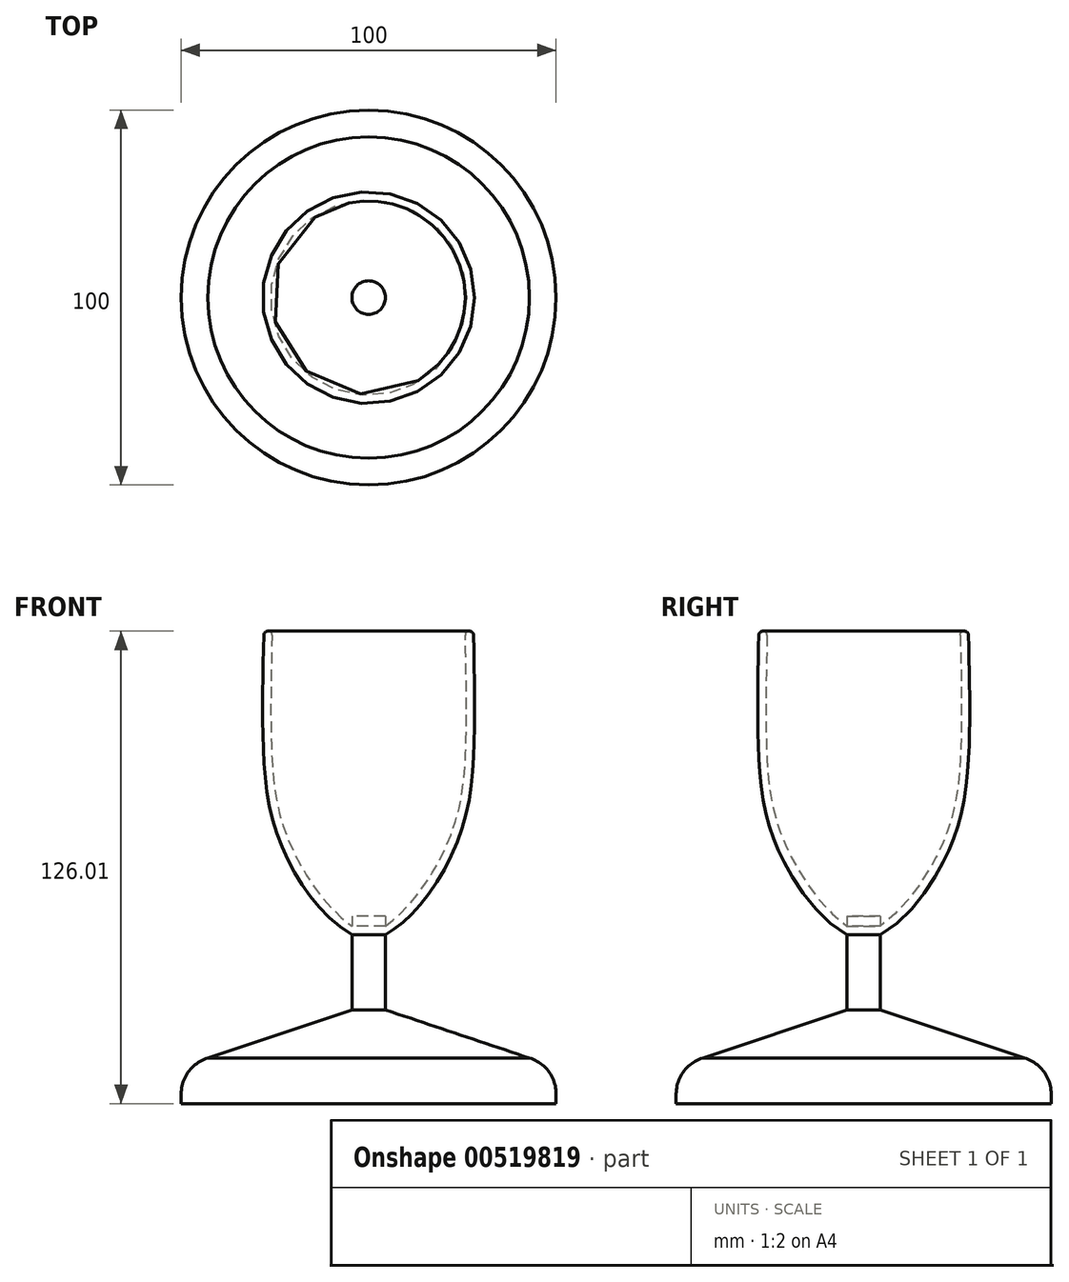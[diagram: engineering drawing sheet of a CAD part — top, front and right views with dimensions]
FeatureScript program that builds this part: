
annotation { "Feature Type Name" : "Feature", "Feature Type Description" : "" }
export const myFeature = defineFeature(function(context is Context, id is Id, definition is map)
    precondition{}
    {
        {
            var Q0;
            Q0=qCreatedBy(makeId("Front.planeOp"),FACE);
            var sketch = newSketch(context, id + "F0", { "sketchPlane" : qUnion([Q0])});
            skLineSegment(sketch, "E0", {"start": v(0, 0) * mm, "end": v(-50, 0) * mm});
            skLineSegment(sketch, "E1", {"start": v(-50, 0) * mm, "end": v(-50, 2.56) * mm});
            skLineSegment(sketch, "E2", {"start": v(0, 25) * mm, "end": v(0, 0) * mm});
            skPoint(sketch, "E3.visualSharp", {"position": v(-50, 10) * mm});
            skArc(sketch, "E3.filletArc", {"start": v(-42.87, 12.14) * mm, "mid": v(-48.02, 8.53) * mm, "end": v(-50, 2.56) * mm});
            skLineSegment(sketch, "E4", {"start": v(0, 25) * mm, "end": v(-4.48, 25) * mm});
            skLineSegment(sketch, "E5", {"start": v(-42.87, 12.14) * mm, "end": v(-4.48, 25) * mm});
            skLineSegment(sketch, "E6", {"start": v(0, 25) * mm, "end": v(0, 42.45) * mm});
            skFitSpline(sketch, "E7", {"points": [v(0, 42.45) * mm, v(-11.37, 50.4) * mm, v(-24.37, 71.7) * mm, v(-28.16, 97.08) * mm, v(-27.93, 126) * mm], "startDerivative": vector(-58.52, 32.33) * mm, "endDerivative": vector(2.55, 104.8) * mm});
            skFitSpline(sketch, "E8", {"points": [v(0, 44.25) * mm, v(-9.7, 51.95) * mm, v(-22.25, 72.4) * mm, v(-25.98, 97.02) * mm, v(-25.73, 126) * mm], "startDerivative": vector(-50.86, 33.35) * mm, "endDerivative": vector(2.52, 103.26) * mm});
            skLineSegment(sketch, "E9", {"start": v(-27.93, 126) * mm, "end": v(-25.73, 126) * mm});
            skLineSegment(sketch, "E10", {"start": v(-4.48, 25) * mm, "end": v(-4.48, 45.02) * mm});
            skLineSegment(sketch, "E11", {"start": v(0, 42.45) * mm, "end": v(0, 44.25) * mm});
            skSolve(sketch);
        }
        {
            var Q0;
            Q0=makeQuery(id+"F0.imprint","IMPRINT",FACE,{"disambiguationData":[TD([[makeQuery(id+"F0.imprint","IMPRINT",EDGE,{"derivedFrom":sQuery(id+"F0.wireOp",EDGE,"E0")}),-1.0]])]});
            var Q1;
            Q1=sQuery(id+"F0.wireOp",EDGE,"E2");
            revolve(context, id + "F1", {"entities" : qUnion([Q0]), "axis" : qUnion([Q1]), "revolveType" : RevolveType.FULL});
        }
        {
            var Q0;
            Q0=makeQuery(id+"F1.opRevolve","SWEPT_FACE",FACE,{"disambiguationData":[OSD([sQuery(id+"F0.wireOp",EDGE,"E4")])]});
            extrude(context, id + "F2", {"entities" : qUnion([Q0]), "operationType" : NewBodyOperationType.ADD, "depth" : 25 * mm, "offsetDistance" : 25 * mm});
        }
        {
            var Q0;
            Q0=makeQuery(id+"F0.imprint","IMPRINT",FACE,{"disambiguationData":[TD([[makeQuery(id+"F0.imprint","IMPRINT",EDGE,{"derivedFrom":sQuery(id+"F0.wireOp",EDGE,"E0")}),-1.0]])]});
            var Q1;
            Q1=makeQuery(id+"F0.imprint","IMPRINT",FACE,{"disambiguationData":[TD([[makeQuery(id+"F0.imprint","IMPRINT",EDGE,{"derivedFrom":sQuery(id+"F0.wireOp",EDGE,"E4")}),-1.0]])]});
            var Q2;
            Q2=makeQuery(id+"F0.imprint","IMPRINT",FACE,{"disambiguationData":[TD([[makeQuery(id+"F0.imprint","IMPRINT",EDGE,{"derivedFrom":sQuery(id+"F0.wireOp",EDGE,"E8")}),1.0]])]});
            var Q3;
            Q3=sQuery(id+"F0.wireOp",EDGE,"E2");
            revolve(context, id + "F3", {"operationType" : NewBodyOperationType.ADD, "entities" : qUnion([Q0, Q1, Q2]), "axis" : qUnion([Q3]), "revolveType" : RevolveType.FULL});
        }
        {
            var Q0;
            Q0=makeQuery(id+"F3.opRevolve","SWEPT_EDGE",EDGE,{"disambiguationData":[OSD([sQuery(id+"F0.wireOp",EDGE,"E7"),sQuery(id+"F0.wireOp",EDGE,"E9")])]});
            var Q1;
            Q1=makeQuery(id+"F3.opRevolve","SWEPT_EDGE",EDGE,{"disambiguationData":[OSD([sQuery(id+"F0.wireOp",EDGE,"E8"),sQuery(id+"F0.wireOp",EDGE,"E9")])]});
            fillet(context, id + "F4", {"entities" : qUnion([Q0, Q1]), "radius" : 1 * mm, "tangentPropagation" : true, "allowEdgeOverflow" : false});
        }
    });
